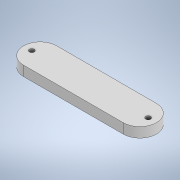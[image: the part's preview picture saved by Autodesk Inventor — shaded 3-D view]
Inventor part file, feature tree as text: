
AUTODESK INVENTOR PART (.ipt)
format: ipt  version: 2022 (Build 260153000, 153)  size: 113,152 bytes
history: native  units: mm
features: extrude x1, sketch x1
ambient origin geometry x8: Origin, YZ Plane, XZ Plane, XY Plane, X Axis, Y Axis, Z Axis, Center Point
bodies: Solid1 (feature_tree)
feature tree (2):
  extrude  "Extrusion1"  Depth=20.0mm
  sketch  "Sketch1"  dims[d0=80.0mm d1=20.0mm d3=35.0mm d4=0.0mm d5=35.0mm d6=180.0deg d7=3.0mm d8=3.0mm d9=6.0mm d10=0.0mm d11=10.0mm]
